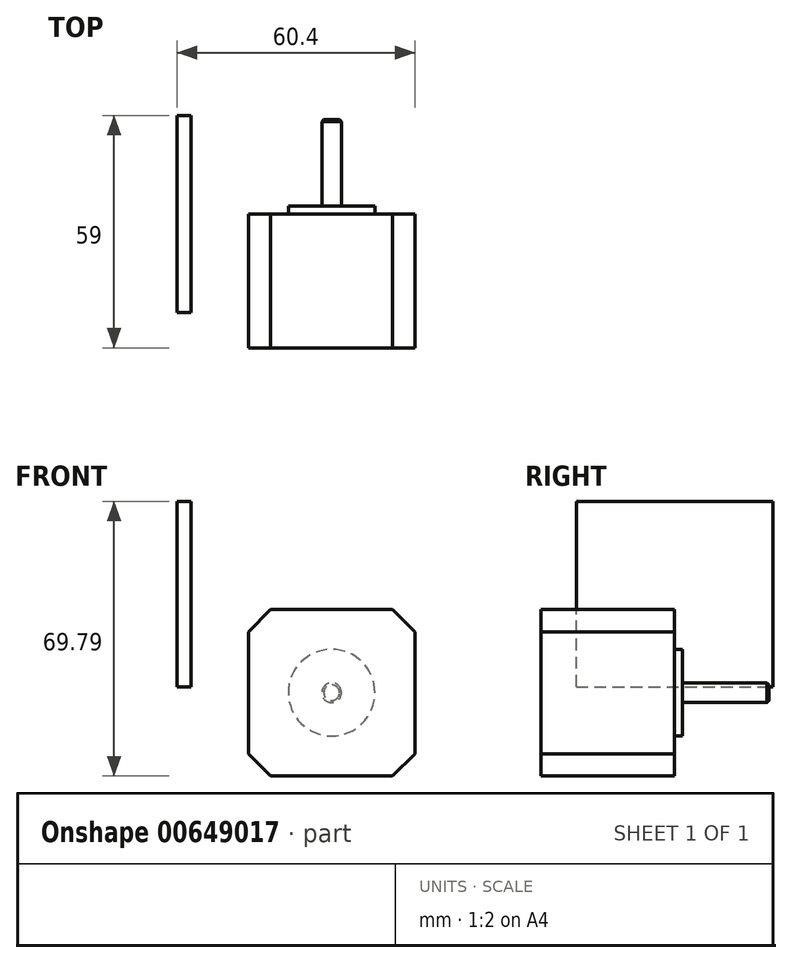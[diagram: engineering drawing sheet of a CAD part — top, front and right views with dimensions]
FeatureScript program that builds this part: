
annotation { "Feature Type Name" : "Feature", "Feature Type Description" : "" }
export const myFeature = defineFeature(function(context is Context, id is Id, definition is map)
    precondition{}
    {
        {
            var Q0;
            Q0=qCreatedBy(makeId("Front.planeOp"),FACE);
            var sketch = newSketch(context, id + "F0", { "sketchPlane" : qUnion([Q0])});
            skLineSegment(sketch, "E0.bottom", {"start": v(21.15, 21.15) * mm, "end": v(-21.15, 21.15) * mm});
            skLineSegment(sketch, "E0.top", {"start": v(21.15, -21.15) * mm, "end": v(-21.15, -21.15) * mm});
            skLineSegment(sketch, "E0.left", {"start": v(21.15, 21.15) * mm, "end": v(21.15, -21.15) * mm});
            skLineSegment(sketch, "E0.right", {"start": v(-21.15, 21.15) * mm, "end": v(-21.15, -21.15) * mm});
            skPoint(sketch, "E0.middle", {"position": v(0, 0) * mm});
            skLineSegment(sketch, "E1", {"start": v(-21.15, 15.5) * mm, "end": v(-15.5, 21.15) * mm});
            skLineSegment(sketch, "E2", {"start": v(15.5, 21.15) * mm, "end": v(21.15, 15.5) * mm});
            skLineSegment(sketch, "E3", {"start": v(21.15, -15.5) * mm, "end": v(15.5, -21.15) * mm});
            skLineSegment(sketch, "E4", {"start": v(-15.5, -21.15) * mm, "end": v(-21.15, -15.5) * mm});
            skSolve(sketch);
        }
        {
            var Q0;
            Q0=qCreatedBy(makeId("Right.planeOp"),FACE);
            var sketch = newSketch(context, id + "F1", { "sketchPlane" : qUnion([Q0])});
            skLineSegment(sketch, "E5", {"start": v(0, 0) * mm, "end": v(-34, 0) * mm});
            skLineSegment(sketch, "E6", {"start": v(-34, 0) * mm, "end": v(-34, 5.53) * mm, "construction": true});
            skSolve(sketch);
        }
        {
            var Q0;
            Q0=qCreatedBy(makeId("Front.planeOp"),FACE);
            var Q1;
            Q1=sQuery(id+"F1.wireOp",VERTEX,"E6.start");
            cPlane(context, id + "F2", {"entities" : qUnion([Q0, Q1]), "cplaneType" : CPlaneType.PLANE_POINT, "offset" : 25 * mm, "width" : 150 * mm, "height" : 150 * mm});
        }
        {
            var Q0;
            {var subQ0=sQuery(id+"F0.wireOp",EDGE,"E1");Q0=makeQuery(id+"F0.imprint","IMPRINT",FACE,{"disambiguationData":[TD([[makeQuery(id+"F0.imprint","IMPRINT",EDGE,{"derivedFrom":subQ0}),-1.0]])]});}
            var Q1;
            Q1=qCreatedBy(id+"F2.planeOp",FACE);
            extrude(context, id + "F3", {"entities" : qUnion([Q0]), "endBound" : BoundingType.UP_TO_SURFACE, "depth" : 34 * mm, "endBoundEntityFace" : qUnion([Q1]), "offsetDistance" : 25 * mm});
        }
        {
            var Q0;
            Q0=qCreatedBy(makeId("Front.planeOp"),FACE);
            var sketch = newSketch(context, id + "F4", { "sketchPlane" : qUnion([Q0])});
            skCircle(sketch, "E7", {"center": v(0, 0) * mm, "radius": 2.5 * mm});
            skSolve(sketch);
        }
        {
            var Q0;
            Q0=qCreatedBy(makeId("Right.planeOp"),FACE);
            var sketch = newSketch(context, id + "F5", { "sketchPlane" : qUnion([Q0])});
            skLineSegment(sketch, "E8", {"start": v(0, 0) * mm, "end": v(24, 0) * mm});
            skLineSegment(sketch, "E9", {"start": v(24, 0) * mm, "end": v(24, 5.27) * mm, "construction": true});
            skSolve(sketch);
        }
        {
            var Q0;
            Q0=sQuery(id+"F5.wireOp",VERTEX,"E8.end");
            var Q1;
            Q1=qCreatedBy(makeId("Front.planeOp"),FACE);
            cPlane(context, id + "F6", {"entities" : qUnion([Q0, Q1]), "cplaneType" : CPlaneType.PLANE_POINT, "offset" : 25 * mm, "width" : 150 * mm, "height" : 150 * mm});
        }
        {
            var Q0;
            Q0 = qSketchRegion(id + "F4", true);
            var Q1;
            Q1=qCreatedBy(id+"F6.planeOp",FACE);
            extrude(context, id + "F7", {"entities" : qUnion([Q0]), "operationType" : NewBodyOperationType.ADD, "endBound" : BoundingType.UP_TO_SURFACE, "oppositeDirection" : true, "depth" : 24 * mm, "endBoundEntityFace" : qUnion([Q1]), "offsetDistance" : 25 * mm});
        }
        {
            var Q0;
            Q0=qCreatedBy(makeId("Front.planeOp"),FACE);
            var sketch = newSketch(context, id + "F8", { "sketchPlane" : qUnion([Q0])});
            skCircle(sketch, "E10", {"center": v(0, 0) * mm, "radius": 11 * mm});
            skSolve(sketch);
        }
        {
            var Q0;
            Q0 = qSketchRegion(id + "F8", true);
            extrude(context, id + "F9", {"entities" : qUnion([Q0]), "operationType" : NewBodyOperationType.ADD, "oppositeDirection" : true, "depth" : 2 * mm, "offsetDistance" : 25 * mm});
        }
        {
            var Q0;
            Q0=makeQuery(id+"F7.opExtrude","CAP_EDGE",EDGE,{"disambiguationData":[OSD([sQuery(id+"F4.wireOp",EDGE,"E7")])],"isStart":false});
            chamfer(context, id + "F10", {"entities" : qUnion([Q0]), "width" : .5 * mm, "tangentPropagation" : true});
        }
        {
            var Q0;
            Q0=qCreatedBy(makeId("Front.planeOp"),FACE);
            var sketch = newSketch(context, id + "F11", { "sketchPlane" : qUnion([Q0])});
            skCircle(sketch, "E11", {"center": v(0, 0) * mm, "radius": 62.5 * mm});
            skCircle(sketch, "E12", {"center": v(0, 0) * mm, "radius": 30 * mm});
            skPoint(sketch, "E13", {"position": v(0, 62.5) * mm});
            skPoint(sketch, "E14", {"position": v(0, -62.5) * mm});
            skPoint(sketch, "E15", {"position": v(-62.5, 0) * mm});
            skPoint(sketch, "E16", {"position": v(62.5, 0) * mm});
            skSolve(sketch);
        }
        {
            var Q0;
            Q0=qCreatedBy(makeId("Right.planeOp"),FACE);
            var sketch = newSketch(context, id + "F12", { "sketchPlane" : qUnion([Q0])});
            skLineSegment(sketch, "E17.bottom", {"start": v(-32.5, 62.5) * mm, "end": v(32.5, 62.5) * mm});
            skLineSegment(sketch, "E17.top", {"start": v(-32.5, -62.5) * mm, "end": v(32.5, -62.5) * mm});
            skLineSegment(sketch, "E17.left", {"start": v(-32.5, 62.5) * mm, "end": v(-32.5, -62.5) * mm});
            skLineSegment(sketch, "E17.right", {"start": v(32.5, 62.5) * mm, "end": v(32.5, -62.5) * mm});
            skPoint(sketch, "E17.middle", {"position": v(0, 0) * mm});
            skLineSegment(sketch, "E18", {"start": v(32.5, 0) * mm, "end": v(0, 0) * mm, "construction": true});
            skLineSegment(sketch, "E19", {"start": v(0, 0) * mm, "end": v(-32.5, 0) * mm, "construction": true});
            skSolve(sketch);
        }
        {
            var Q0;
            Q0=qCreatedBy(makeId("Front.planeOp"),FACE);
            var sketch = newSketch(context, id + "F13", { "sketchPlane" : qUnion([Q0])});
            skLineSegment(sketch, "E20", {"start": v(-37.5, 50) * mm, "end": v(-37.5, -50) * mm, "construction": true});
            skCircle(sketch, "E21", {"center": v(-37.5, -3.28) * mm, "radius": 2.5 * mm});
            skCircle(sketch, "E22", {"center": v(-37.5, 3.28) * mm, "radius": 2.5 * mm});
            skLineSegment(sketch, "E23", {"start": v(-37.5, -3.28) * mm, "end": v(-37.5, 3.28) * mm});
            skPoint(sketch, "E24", {"position": v(-37.5, 0) * mm});
            skLineSegment(sketch, "E25", {"start": v(-37.5, 3.28) * mm, "end": v(0, 0) * mm});
            skLineSegment(sketch, "E26", {"start": v(0, 0) * mm, "end": v(-37.5, -3.28) * mm});
            skSolve(sketch);
        }
        {
            var Q0;
            Q0=qCreatedBy(makeId("Front.planeOp"),FACE);
            var sketch = newSketch(context, id + "F14", { "sketchPlane" : qUnion([Q0])});
            skLineSegment(sketch, "E27.bottom", {"start": v(-39.25, 1.53) * mm, "end": v(-35.75, 1.53) * mm});
            skLineSegment(sketch, "E27.top", {"start": v(-39.25, 48.64) * mm, "end": v(-35.75, 48.64) * mm});
            skLineSegment(sketch, "E27.left", {"start": v(-39.25, 1.53) * mm, "end": v(-39.25, 48.64) * mm});
            skLineSegment(sketch, "E27.right", {"start": v(-35.75, 1.53) * mm, "end": v(-35.75, 48.64) * mm});
            skCircle(sketch, "E28", {"center": v(-37.5, 3.28) * mm, "radius": 1.75 * mm});
            skPoint(sketch, "E28.centerSnap0", {"position": v(-37.5, 1.53) * mm});
            skSolve(sketch);
        }
        {
            var Q0;
            Q0 = qSketchRegion(id + "F14", true);
            extrude(context, id + "F15", {"entities" : qUnion([Q0]), "endBound" : BoundingType.SYMMETRIC, "depth" : 50 * mm, "offsetDistance" : 25 * mm});
        }
    });
